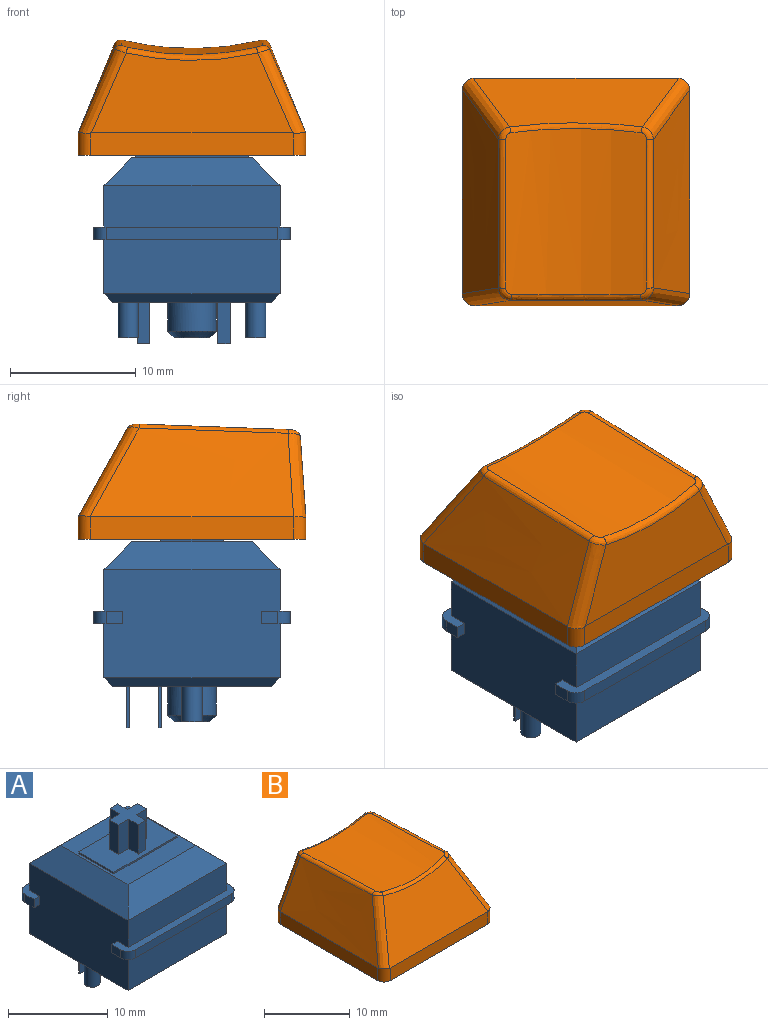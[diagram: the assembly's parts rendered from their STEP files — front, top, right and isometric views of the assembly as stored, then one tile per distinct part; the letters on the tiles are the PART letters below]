
ASSEMBLY  parts=2 mates=1
PART A: 69 faces, bbox 15.6x15.6x18.6 mm
  f0: plane 15.6x2.3mm, normal (0,0,-1), area 14.4mm2, adj f2,f3,f28,f30,f35,f60,f62,f63
  f1: plane 15.6x2.3mm, normal (0,0,-1), area 14.4mm2, adj f28,f30,f33,f34,f36,f59,f61,f64
  f2: plane 1.3x1mm, normal (1,0,0), area 1.3mm2, adj f0,f32,f62,f66
  f3: plane 1.3x1mm, normal (-1,0,0), area 1.3mm2, adj f0,f32,f63,f68
  f4: plane 15.6x2.3mm, normal (0,0,1), area 14.4mm2, adj f28,f30,f31,f33,f34,f36,f61,f64
  f5: plane 14x2.2mm, normal (-0.71,0,0.71), area 36.7mm2, adj f6,f7,f26,f30
  f6: plane 14x2.2mm, normal (0,-0.71,0.71), area 36.7mm2, adj f5,f7,f27,f31
  f7: plane 9.6x9.6mm, normal (0,0,1), area 47.2mm2, adj f5,f6,f8,f9,f10,f11,f26,f27
  f8: plane 5x0.2mm, normal (1,0,0), area 1mm2, adj f7,f9,f11,f12
  f9: plane 9x0.2mm, normal (0,1,0), area 1.8mm2, adj f7,f8,f10,f12
  f10: plane 5x0.2mm, normal (-1,0,0), area 1mm2, adj f7,f9,f11,f12
  f11: plane 9x0.2mm, normal (0,-1,0), area 1.8mm2, adj f7,f8,f10,f12
  f12: plane 9x5mm, normal (0,0,1), area 36.9mm2, adj f8,f9,f10,f11,f13,f14,f15,f16
  f13: plane 3.6x1.35mm, normal (1,0,0), area 4.9mm2, adj f12,f14,f24,f25
  f14: plane 3.6x1.08mm, normal (0,1,0), area 3.9mm2, adj f12,f13,f15,f25
  f15: plane 3.6x1.35mm, normal (-1,0,0), area 4.9mm2, adj f12,f14,f16,f25
  f16: plane 3.6x1.46mm, normal (0,1,0), area 5.3mm2, adj f12,f15,f17,f25
  f17: plane 3.6x1.3mm, normal (-1,0,0), area 4.7mm2, adj f12,f16,f18,f25
  f18: plane 3.6x1.46mm, normal (0,-1,0), area 5.3mm2, adj f12,f17,f19,f25
  f19: plane 3.6x1.35mm, normal (-1,0,0), area 4.9mm2, adj f12,f18,f20,f25
  f20: plane 3.6x1.08mm, normal (0,-1,0), area 3.9mm2, adj f12,f19,f21,f25
  f21: plane 3.6x1.35mm, normal (1,0,0), area 4.9mm2, adj f12,f20,f22,f25
  f22: plane 3.6x1.46mm, normal (0,-1,0), area 5.3mm2, adj f12,f21,f23,f25
  f23: plane 3.6x1.3mm, normal (1,0,0), area 4.7mm2, adj f12,f22,f24,f25
  f24: plane 3.6x1.46mm, normal (0,1,0), area 5.3mm2, adj f12,f13,f23,f25
  f25: plane 4x4mm, normal (0,0,1), area 8.1mm2, adj f13,f14,f15,f16,f17,f18,f19,f20
  f26: plane 14x2.2mm, normal (0,0.71,0.71), area 36.7mm2, adj f5,f7,f27,f29
  f27: plane 14x2.2mm, normal (0.71,0,0.71), area 36.7mm2, adj f6,f7,f26,f28
  f28: plane 14x8.6mm, normal (1,0,0), area 117.4mm2, adj f0,f1,f4,f27,f29,f31,f32,f55
  f29: plane 14x3.3mm, normal (0,1,0), area 46.2mm2, adj f26,f28,f30,f32
  f30: plane 14x8.6mm, normal (-1,0,0), area 117.4mm2, adj f0,f1,f4,f5,f29,f31,f32,f57
  f31: plane 14x3.3mm, normal (0,-1,0), area 46.2mm2, adj f4,f6,f28,f30
  f32: plane 15.6x2.3mm, normal (0,0,1), area 14.4mm2, adj f2,f3,f28,f29,f30,f35,f62,f63
  f33: plane 13.6x1mm, normal (0,-1,0), area 13.6mm2, adj f1,f4,f61,f64
  f34: plane 1.3x1mm, normal (1,0,0), area 1.3mm2, adj f1,f4,f61,f65
  f35: plane 13.6x1mm, normal (0,1,0), area 13.6mm2, adj f0,f32,f62,f63
  f36: plane 1.3x1mm, normal (-1,0,0), area 1.3mm2, adj f1,f4,f64,f67
  f37: plane 2.85x2.85mm, normal (0,0,-1), area 6.4mm2, adj f38
  f38: cone r=1.43mm half-angle=45deg, axis (0,0,1), area 7.4mm2, adj f37,f43
  f39: plane 1x0.2mm, normal (0,0,-1), area 0.2mm2, adj f44,f45,f46,f47
  f40: plane 1x0.2mm, normal (0,0,-1), area 0.2mm2, adj f48,f49,f50,f51
  f41: plane 1.6x1.6mm, normal (0,0,-1), area 2mm2, adj f52
  f42: plane 1.6x1.6mm, normal (0,0,-1), area 2mm2, adj f53
  f43: cylinder r=1.93mm len=3.85mm, axis (0,0,1), area 27.8mm2, adj f38,f54
  f44: plane 3.3x0.2mm, normal (-1,0,0), area 0.7mm2, adj f39,f45,f47,f54
  f45: plane 3.3x1mm, normal (0,1,0), area 3.3mm2, adj f39,f44,f46,f54
  f46: plane 3.3x0.2mm, normal (1,0,0), area 0.7mm2, adj f39,f45,f47,f54
  f47: plane 3.3x1mm, normal (0,-1,0), area 3.3mm2, adj f39,f44,f46,f54
  f48: plane 3.3x0.2mm, normal (-1,0,0), area 0.7mm2, adj f40,f49,f51,f54
  f49: plane 3.3x1mm, normal (0,1,0), area 3.3mm2, adj f40,f48,f50,f54
  f50: plane 3.3x0.2mm, normal (1,0,0), area 0.7mm2, adj f40,f49,f51,f54
  f51: plane 3.3x1mm, normal (0,-1,0), area 3.3mm2, adj f40,f48,f50,f54
  f52: cylinder r=0.8mm len=2.8mm, axis (0,0,1), area 14.1mm2, adj f41,f54
  f53: cylinder r=0.8mm len=2.8mm, axis (0,0,1), area 14.1mm2, adj f42,f54
  f54: plane 12.6x12.6mm, normal (0,0,-1), area 142.7mm2, adj f43,f44,f45,f46,f47,f48,f49,f50
  f55: plane 14x0.7mm, normal (0.71,0,-0.71), area 13.2mm2, adj f28,f54,f56,f58
  f56: plane 14x0.7mm, normal (0,0.71,-0.71), area 13.2mm2, adj f54,f55,f57,f60
  f57: plane 14x0.7mm, normal (-0.71,0,-0.71), area 13.2mm2, adj f30,f54,f56,f58
  f58: plane 14x0.7mm, normal (0,-0.71,-0.71), area 13.2mm2, adj f54,f55,f57,f59
  f59: plane 14x4.3mm, normal (0,-1,0), area 60.2mm2, adj f1,f28,f30,f58
  f60: plane 14x4.3mm, normal (0,1,0), area 60.2mm2, adj f0,f28,f30,f56
  f61: cylinder r=1mm len=1mm, axis (0,0,-1), area 1.6mm2, adj f1,f4,f33,f34
  f62: cylinder r=1mm len=1mm, axis (0,0,1), area 1.6mm2, adj f0,f2,f32,f35
  f63: cylinder r=1mm len=1mm, axis (0,0,-1), area 1.6mm2, adj f0,f3,f32,f35
  f64: cylinder r=1mm len=1mm, axis (0,0,1), area 1.6mm2, adj f1,f4,f33,f36
  f65: plane 1x0.8mm, normal (0,1,0), area 0.8mm2, adj f1,f4,f28,f34
  f66: plane 1x0.8mm, normal (0,-1,0), area 0.8mm2, adj f0,f2,f28,f32
  f67: plane 1x0.8mm, normal (0,1,0), area 0.8mm2, adj f1,f4,f30,f36
  f68: plane 1x0.8mm, normal (0,-1,0), area 0.8mm2, adj f0,f3,f30,f32
PART B: 50 faces, bbox 21.6x22.4x13.2 mm
  f0: plane 18.1x18.1mm, normal (0,0,-1), area 67.5mm2, adj f1,f2,f3,f4,f10,f12,f14,f16
  f1: plane 16.1x1.8mm, normal (1,0,0), area 29mm2, adj f0,f8,f10,f16
  f2: plane 16.11x1.81mm, normal (0,1,0), area 29mm2, adj f0,f5,f14,f15,f16,f17
  f3: plane 16.1x1.8mm, normal (-1,0,0), area 29mm2, adj f0,f6,f12,f14
  f4: plane 16.1x1.8mm, normal (0,-1,0), area 29mm2, adj f0,f7,f10,f12
  f5: plane 15.98x6.33mm, normal (0,1,0.07), area 79.8mm2, adj f2,f15,f17,f20
  f6: bspline ~18.1x7.49mm, area 104.4mm2, adj f3,f12,f13,f14,f15,f19
  f7: plane 16.33x7.03mm, normal (0,-0.87,0.48), area 103.3mm2, adj f4,f10,f11,f12,f13,f23
  f8: bspline ~18.1x7.49mm, area 104.4mm2, adj f1,f10,f11,f16,f17,f24
  f9: cylinder r=22.9mm len=12.87mm, axis (0,1,-0.04), area 144.5mm2, adj f18,f19,f20,f21,f22,f23,f24,f25
  f10: cylinder r=1mm len=1.88mm, axis (0,0,-1), area 2.9mm2, adj f0,f1,f4,f7,f8,f11
  f11: bspline ~9.11x5.74mm, area 11.9mm2, adj f7,f8,f10,f25
  f12: cylinder r=1mm len=1.88mm, axis (0,0,1), area 2.9mm2, adj f0,f3,f4,f6,f7,f13
  f13: bspline ~9.11x5.74mm, area 11.9mm2, adj f6,f7,f12,f21
  f14: cylinder r=1mm len=1.81mm, axis (0,0,-1), area 2.8mm2, adj f0,f2,f3,f6,f15
  f15: bspline ~11.15x5.6mm, area 11mm2, adj f2,f5,f6,f14,f18
  f16: cylinder r=1mm len=1.81mm, axis (0,0,1), area 2.8mm2, adj f0,f1,f2,f8,f17
  f17: bspline ~11.16x5.6mm, area 11mm2, adj f2,f5,f8,f16,f22
  f18: bspline ~1.21x1.09mm, area 0.9mm2, adj f9,f15,f19,f20
  f19: bspline ~17.91x1.05mm, area 8.4mm2, adj f6,f9,f18,f21
  f20: bspline ~10.48x1.05mm, area 7.6mm2, adj f5,f9,f18,f22
  f21: bspline ~1.23x1.13mm, area 0.7mm2, adj f9,f13,f19,f23
  f22: bspline ~1.25x1.04mm, area 0.9mm2, adj f9,f17,f20,f24
  f23: bspline ~10.58x0.84mm, area 5.8mm2, adj f7,f9,f21,f25
  f24: bspline ~17.91x1.05mm, area 8.4mm2, adj f8,f9,f22,f25
  f25: bspline ~1.23x1.02mm, area 0.7mm2, adj f9,f11,f23,f24
  f26: plane 16.11x1.61mm, normal (-1,0,0), area 25.7mm2, adj f0,f27,f29,f32,f33
  f27: plane 16.1x1.77mm, normal (0,-1,0), area 28.4mm2, adj f0,f26,f28,f30,f31,f33
  f28: plane 16.11x1.61mm, normal (1,0,0), area 25.7mm2, adj f0,f27,f29,f31,f32
  f29: plane 16.1x1.54mm, normal (0,1,0), area 24.8mm2, adj f0,f26,f28,f32
  f30: plane 16.08x6.01mm, normal (0,-1,-0.07), area 74.4mm2, adj f27,f31,f33,f34
  f31: offset ~20.1x9.49mm, area 95.9mm2, adj f27,f28,f30,f32,f34
  f32: plane 16.73x7.17mm, normal (0,0.87,-0.48), area 95.8mm2, adj f26,f28,f29,f31,f33,f34
  f33: offset ~20.1x9.49mm, area 95.9mm2, adj f26,f27,f30,f32,f34
  f34: cylinder r=23.9mm len=12.1mm, axis (0,1,-0.04), area 108.1mm2, adj f30,f31,f32,f33,f46
  f35: plane 7.29x1.35mm, normal (-1,0,0), area 9.8mm2, adj f36,f44,f45,f49
  f36: plane 7.37x1.5mm, normal (0,-1,0), area 11mm2, adj f35,f37,f45,f49
  f37: plane 7.41x1.3mm, normal (-1,0,0), area 9.6mm2, adj f36,f38,f45,f49
  f38: plane 7.41x1.5mm, normal (0,1,0), area 11mm2, adj f37,f39,f45,f49
  f39: plane 7.38x1.35mm, normal (-1,0,0), area 9.9mm2, adj f38,f40,f45,f49
  f40: plane 7.38x1mm, normal (0,1,0), area 7.4mm2, adj f39,f41,f45,f49
  f41: plane 7.38x1.35mm, normal (1,0,0), area 9.9mm2, adj f40,f42,f45,f49
  f42: plane 7.41x1.5mm, normal (0,1,0), area 11mm2, adj f41,f43,f45,f49
  f43: plane 7.41x1.3mm, normal (1,0,0), area 9.6mm2, adj f42,f45,f47,f49
  f44: plane 7.24x1mm, normal (0,-1,0), area 7.2mm2, adj f35,f45,f48,f49
  f45: plane 5.5x5.5mm, normal (0,0,-1), area 15.9mm2, adj f35,f36,f37,f38,f39,f40,f41,f42
  f46: cylinder r=2.75mm len=7.46mm, axis (0,0,-1), area 129mm2, adj f34,f45
  f47: plane 7.37x1.5mm, normal (0,-1,0), area 11mm2, adj f43,f45,f48,f49
  f48: plane 7.29x1.35mm, normal (1,0,0), area 9.8mm2, adj f44,f45,f47,f49
  f49: cylinder r=23.9mm len=4mm, axis (0,1,-0.04), area 7.9mm2, adj f35,f36,f37,f38,f39,f40,f41,f42
PLACE A at identity fixed
PLACE B rot(axis=(0,0,1),180deg) t=(0,0,11.7)mm
MATE fastened A.f38 <-> B.f46  axis (0,0,1) through (0,0,11.7)mm
